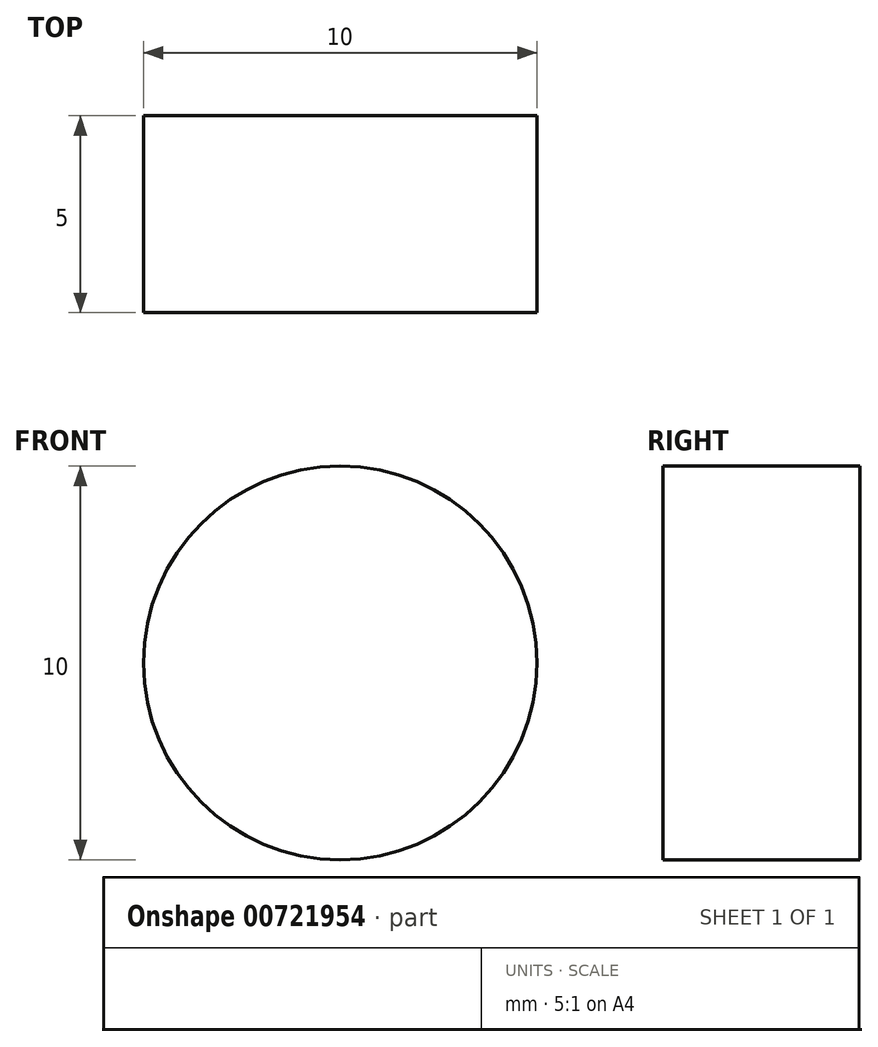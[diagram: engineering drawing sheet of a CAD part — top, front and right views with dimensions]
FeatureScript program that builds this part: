
annotation { "Feature Type Name" : "Feature", "Feature Type Description" : "" }
export const myFeature = defineFeature(function(context is Context, id is Id, definition is map)
    precondition{}
    {
        {
            var Q0;
            Q0=qCreatedBy(makeId("Front.planeOp"),FACE);
            var sketch = newSketch(context, id + "F0", { "sketchPlane" : qUnion([Q0])});
            skCircle(sketch, "E0", {"center": v(0, 0) * mm, "radius": 5 * mm});
            skSolve(sketch);
        }
        {
            var Q0;
            Q0=qSketchRegion(id+"F0",true);
            extrude(context, id + "F1", {"entities" : qUnion([Q0]), "depth" : 5 * mm, "offsetDistance" : 25 * mm});
        }
    });
